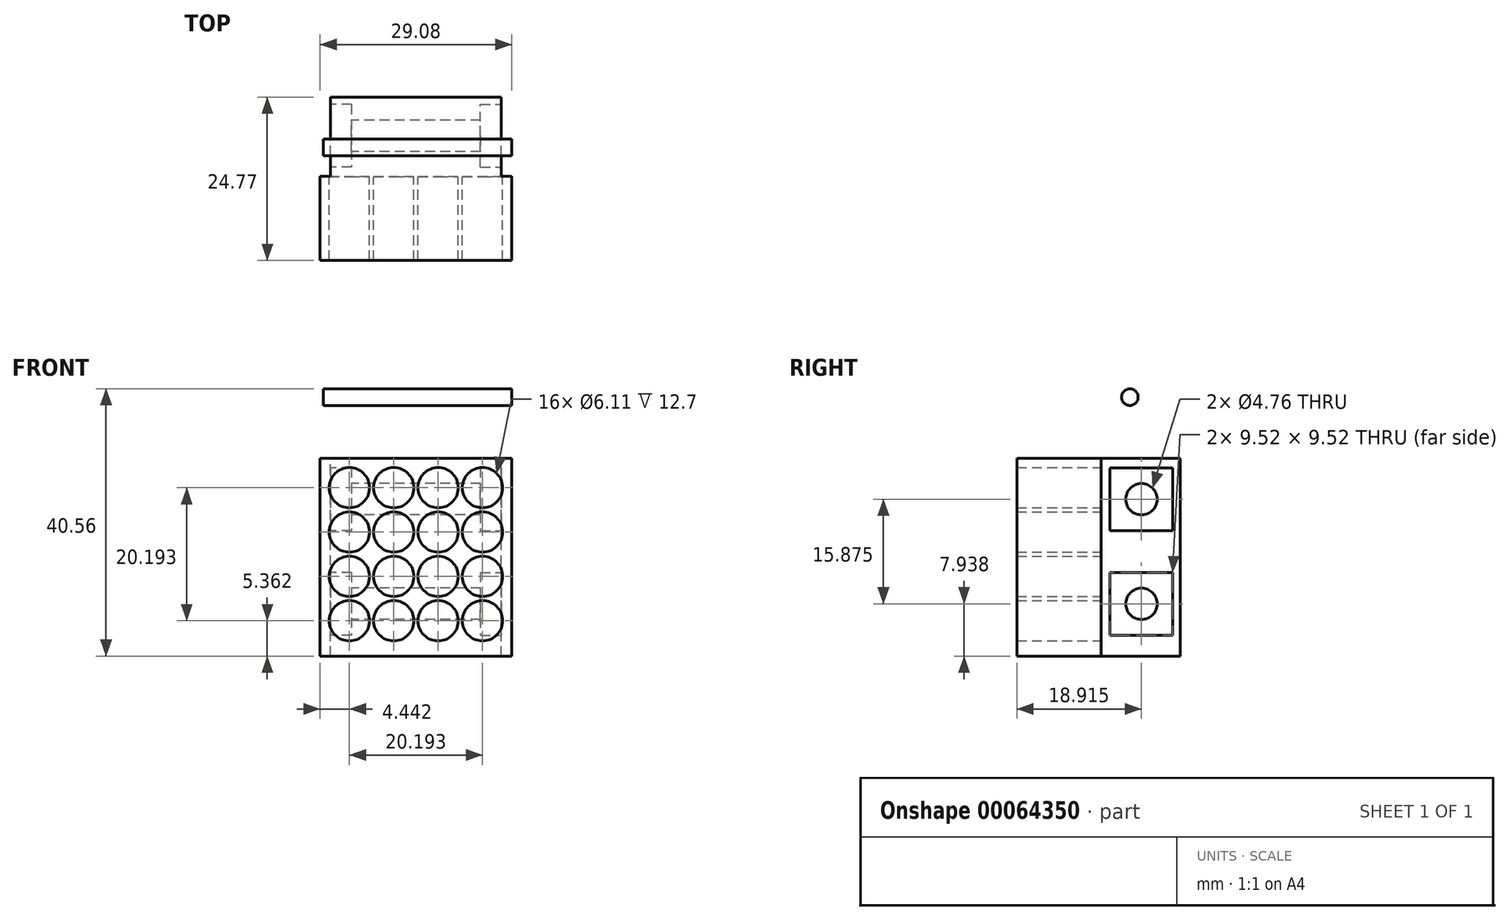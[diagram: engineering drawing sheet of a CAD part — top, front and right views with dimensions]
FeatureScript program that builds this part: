
annotation { "Feature Type Name" : "Feature", "Feature Type Description" : "" }
export const myFeature = defineFeature(function(context is Context, id is Id, definition is map)
    precondition{}
    {
        {
            var Q0;
            Q0=qCreatedBy(makeId("Front.planeOp"),FACE);
            var sketch = newSketch(context, id + "F0", { "sketchPlane" : qUnion([Q0])});
            skLineSegment(sketch, "E0.bottom", {"start": v(0, 0) * mm, "end": v(-29.08, 0) * mm});
            skLineSegment(sketch, "E0.top", {"start": v(0, 30) * mm, "end": v(-29.08, 30) * mm});
            skLineSegment(sketch, "E0.left", {"start": v(0, 0) * mm, "end": v(0, 30) * mm});
            skLineSegment(sketch, "E0.right", {"start": v(-29.08, 0) * mm, "end": v(-29.08, 30) * mm});
            skCircle(sketch, "E1", {"center": v(-4.45, 25.55) * mm, "radius": 3.06 * mm});
            skCircle(sketch, "E2.0.1.0", {"center": v(-4.45, 18.82) * mm, "radius": 3.06 * mm});
            skCircle(sketch, "E2.0.2.0", {"center": v(-4.45, 12.1) * mm, "radius": 3.06 * mm});
            skCircle(sketch, "E2.1.0.0", {"center": v(-11.18, 25.55) * mm, "radius": 3.06 * mm});
            skCircle(sketch, "E2.1.1.0", {"center": v(-11.18, 18.82) * mm, "radius": 3.06 * mm});
            skCircle(sketch, "E2.1.2.0", {"center": v(-11.18, 12.1) * mm, "radius": 3.06 * mm});
            skCircle(sketch, "E2.2.0.0", {"center": v(-17.9, 25.55) * mm, "radius": 3.06 * mm});
            skCircle(sketch, "E2.2.1.0", {"center": v(-17.9, 18.82) * mm, "radius": 3.06 * mm});
            skCircle(sketch, "E2.2.2.0", {"center": v(-17.9, 12.1) * mm, "radius": 3.06 * mm});
            skLineSegment(sketch, "E2.direction1", {"start": v(-4.45, 25.55) * mm, "end": v(-11.18, 25.55) * mm, "construction": true});
            skLineSegment(sketch, "E2.direction2", {"start": v(-4.45, 25.55) * mm, "end": v(-4.45, 18.82) * mm, "construction": true});
            skCircle(sketch, "E3.0.3.0", {"center": v(-24.64, 25.55) * mm, "radius": 3.06 * mm});
            skCircle(sketch, "E3.0.3.1", {"center": v(-24.64, 18.82) * mm, "radius": 3.06 * mm});
            skCircle(sketch, "E3.0.3.2", {"center": v(-24.64, 12.1) * mm, "radius": 3.06 * mm});
            skCircle(sketch, "E4.0.0.3", {"center": v(-4.45, 5.36) * mm, "radius": 3.06 * mm});
            skCircle(sketch, "E4.0.1.3", {"center": v(-11.18, 5.36) * mm, "radius": 3.06 * mm});
            skCircle(sketch, "E4.0.2.3", {"center": v(-17.9, 5.36) * mm, "radius": 3.06 * mm});
            skCircle(sketch, "E4.0.3.3", {"center": v(-24.64, 5.36) * mm, "radius": 3.06 * mm});
            skLineSegment(sketch, "E5", {"start": v(-29.08, 15) * mm, "end": v(0, 15) * mm, "construction": true});
            skSolve(sketch);
        }
        {
            var Q0;
            Q0=makeQuery(id+"F0.imprint","IMPRINT",FACE,{"disambiguationData":[TD([[makeQuery(id+"F0.imprint","IMPRINT",EDGE,{"derivedFrom":sQuery(id+"F0.wireOp",EDGE,"E0.bottom")}),-1.0]])]});
            extrude(context, id + "F1", {"entities" : qUnion([Q0]), "depth" : 12.7 * mm, "offsetDistance" : 25.4 * mm});
        }
        {
            var Q0;
            Q0=makeQuery(id+"F1.opExtrude","CAP_FACE",FACE,{"disambiguationData":[OSD([sQuery(id+"F0.wireOp",EDGE,"E0.bottom"),sQuery(id+"F0.wireOp",EDGE,"E0.top"),sQuery(id+"F0.wireOp",EDGE,"E0.left"),sQuery(id+"F0.wireOp",EDGE,"E0.right"),sQuery(id+"F0.wireOp",EDGE,"E1"),sQuery(id+"F0.wireOp",EDGE,"E2.0.1.0"),sQuery(id+"F0.wireOp",EDGE,"E2.0.2.0"),sQuery(id+"F0.wireOp",EDGE,"E2.1.0.0"),sQuery(id+"F0.wireOp",EDGE,"E2.1.1.0"),sQuery(id+"F0.wireOp",EDGE,"E2.1.2.0"),sQuery(id+"F0.wireOp",EDGE,"E2.2.0.0"),sQuery(id+"F0.wireOp",EDGE,"E2.2.1.0"),sQuery(id+"F0.wireOp",EDGE,"E2.2.2.0")])],"isStart":true});
            var sketch = newSketch(context, id + "F2", { "sketchPlane" : qUnion([Q0])});
            skLineSegment(sketch, "E6.bottom", {"start": v(0, 30) * mm, "end": v(29.08, 30) * mm});
            skLineSegment(sketch, "E6.top", {"start": v(0, 0) * mm, "end": v(29.08, 0) * mm});
            skLineSegment(sketch, "E6.left", {"start": v(0, 30) * mm, "end": v(0, 0) * mm});
            skLineSegment(sketch, "E6.right", {"start": v(29.08, 30) * mm, "end": v(29.08, 0) * mm});
            skSolve(sketch);
        }
        {
            var Q0;
            Q0=qSketchRegion(id+"F2",true);
            extrude(context, id + "F3", {"entities" : qUnion([Q0]), "operationType" : NewBodyOperationType.ADD, "depth" : 12.06 * mm, "offsetDistance" : 25.4 * mm});
        }
        {
            var Q0;
            Q0=makeQuery(id+"F3.boolean.opBoolean","MERGE",FACE,{"derivedFrom":[makeQuery(id+"F1.opExtrude","SWEPT_FACE",FACE,{"disambiguationData":[OSD([sQuery(id+"F0.wireOp",EDGE,"E0.left")])]}),makeQuery(id+"F3.opExtrude","SWEPT_FACE",FACE,{"disambiguationData":[OSD([sQuery(id+"F2.wireOp",EDGE,"E6.left")])]})]});
            var sketch = newSketch(context, id + "F4", { "sketchPlane" : qUnion([Q0])});
            skLineSegment(sketch, "E7.bottom", {"start": v(0.07, 0) * mm, "end": v(12.07, 0) * mm});
            skLineSegment(sketch, "E7.top", {"start": v(0.07, 30) * mm, "end": v(12.07, 30) * mm});
            skLineSegment(sketch, "E7.left", {"start": v(0.07, 0) * mm, "end": v(0.07, 30) * mm});
            skLineSegment(sketch, "E7.right", {"start": v(12.07, 0) * mm, "end": v(12.07, 30) * mm});
            skSolve(sketch);
        }
        {
            var Q0;
            Q0=qSketchRegion(id+"F4",true);
            extrude(context, id + "F5", {"entities" : qUnion([Q0]), "operationType" : NewBodyOperationType.REMOVE, "oppositeDirection" : true, "depth" : 1.59 * mm});
        }
        {
            var Q0;
            Q0=makeQuery(id+"F3.boolean.opBoolean","MERGE",FACE,{"derivedFrom":[makeQuery(id+"F1.opExtrude","SWEPT_FACE",FACE,{"disambiguationData":[OSD([sQuery(id+"F0.wireOp",EDGE,"E0.right")])]}),makeQuery(id+"F3.opExtrude","SWEPT_FACE",FACE,{"disambiguationData":[OSD([sQuery(id+"F2.wireOp",EDGE,"E6.right")])]})]});
            var sketch = newSketch(context, id + "F6", { "sketchPlane" : qUnion([Q0])});
            skLineSegment(sketch, "E8.bottom", {"start": v(-12.06, 0) * mm, "end": v(-0.06, 0) * mm});
            skLineSegment(sketch, "E8.top", {"start": v(-12.07, 30) * mm, "end": v(-0.07, 30) * mm});
            skLineSegment(sketch, "E8.left", {"start": v(-12.06, 0) * mm, "end": v(-12.07, 30) * mm});
            skLineSegment(sketch, "E8.right", {"start": v(-0.06, 0) * mm, "end": v(-0.07, 30) * mm});
            skSolve(sketch);
        }
        {
            var Q0;
            Q0=qSketchRegion(id+"F6",true);
            extrude(context, id + "F7", {"entities" : qUnion([Q0]), "operationType" : NewBodyOperationType.REMOVE, "oppositeDirection" : true, "depth" : 1.59 * mm});
        }
        {
            var Q0;
            Q0=makeQuery(id+"F7.boolean.opBoolean","COPY",FACE,{"derivedFrom":makeQuery(id+"F7.opExtrude","CAP_FACE",FACE,{"disambiguationData":[OSD([sQuery(id+"F6.wireOp",EDGE,"E8.bottom"),sQuery(id+"F6.wireOp",EDGE,"E8.top"),sQuery(id+"F6.wireOp",EDGE,"E8.left"),sQuery(id+"F6.wireOp",EDGE,"E8.right")])],"isStart":false})});
            var sketch = newSketch(context, id + "F8", { "sketchPlane" : qUnion([Q0])});
            skCircle(sketch, "E9", {"center": v(-6.21, 23.81) * mm, "radius": 2.38 * mm});
            skCircle(sketch, "E10", {"center": v(-6.21, 7.94) * mm, "radius": 2.38 * mm});
            skLineSegment(sketch, "E11", {"start": v(-6.22, 30) * mm, "end": v(-6.21, 0) * mm, "construction": true});
            skPoint(sketch, "E12", {"position": v(-6.22, 30) * mm});
            skSolve(sketch);
        }
        {
            var Q0;
            Q0=qSketchRegion(id+"F8",true);
            extrude(context, id + "F9", {"entities" : qUnion([Q0]), "operationType" : NewBodyOperationType.REMOVE, "endBound" : BoundingType.THROUGH_ALL, "oppositeDirection" : true, "depth" : 25.4 * mm});
        }
        {
            var Q0;
            Q0=makeQuery(id+"F7.boolean.opBoolean","COPY",FACE,{"derivedFrom":makeQuery(id+"F7.opExtrude","CAP_FACE",FACE,{"disambiguationData":[OSD([sQuery(id+"F6.wireOp",EDGE,"E8.bottom"),sQuery(id+"F6.wireOp",EDGE,"E8.top"),sQuery(id+"F6.wireOp",EDGE,"E8.left"),sQuery(id+"F6.wireOp",EDGE,"E8.right")])],"isStart":false})});
            var sketch = newSketch(context, id + "F10", { "sketchPlane" : qUnion([Q0])});
            skLineSegment(sketch, "E13.bottom", {"start": v(-10.98, 28.57) * mm, "end": v(-1.45, 28.57) * mm});
            skLineSegment(sketch, "E13.top", {"start": v(-10.98, 19.05) * mm, "end": v(-1.45, 19.05) * mm});
            skLineSegment(sketch, "E13.left", {"start": v(-10.98, 28.57) * mm, "end": v(-10.98, 19.05) * mm});
            skLineSegment(sketch, "E13.right", {"start": v(-1.45, 28.57) * mm, "end": v(-1.45, 19.05) * mm});
            skPoint(sketch, "E13.middle", {"position": v(-6.21, 23.81) * mm});
            skLineSegment(sketch, "E14.bottom", {"start": v(-10.98, 12.7) * mm, "end": v(-1.45, 12.7) * mm});
            skLineSegment(sketch, "E14.top", {"start": v(-10.98, 3.18) * mm, "end": v(-1.45, 3.18) * mm});
            skLineSegment(sketch, "E14.left", {"start": v(-10.98, 12.7) * mm, "end": v(-10.98, 3.18) * mm});
            skLineSegment(sketch, "E14.right", {"start": v(-1.45, 12.7) * mm, "end": v(-1.45, 3.18) * mm});
            skPoint(sketch, "E14.middle", {"position": v(-6.21, 7.94) * mm});
            skPoint(sketch, "E14.cornerSnap0", {"position": v(-10.98, 23.81) * mm});
            skSolve(sketch);
        }
        {
            var Q0;
            Q0=makeQuery(id+"F5.boolean.opBoolean","COPY",FACE,{"derivedFrom":makeQuery(id+"F5.opExtrude","CAP_FACE",FACE,{"disambiguationData":[OSD([sQuery(id+"F4.wireOp",EDGE,"E7.bottom"),sQuery(id+"F4.wireOp",EDGE,"E7.top"),sQuery(id+"F4.wireOp",EDGE,"E7.left"),sQuery(id+"F4.wireOp",EDGE,"E7.right")])],"isStart":false})});
            var sketch = newSketch(context, id + "F11", { "sketchPlane" : qUnion([Q0])});
            skLineSegment(sketch, "E15.bottom", {"start": v(1.45, 28.58) * mm, "end": v(10.98, 28.58) * mm});
            skLineSegment(sketch, "E15.top", {"start": v(1.45, 19.05) * mm, "end": v(10.98, 19.05) * mm});
            skLineSegment(sketch, "E15.left", {"start": v(1.45, 28.58) * mm, "end": v(1.45, 19.05) * mm});
            skLineSegment(sketch, "E15.right", {"start": v(10.98, 28.58) * mm, "end": v(10.98, 19.05) * mm});
            skPoint(sketch, "E15.middle", {"position": v(6.21, 23.81) * mm});
            skLineSegment(sketch, "E16.bottom", {"start": v(1.45, 12.7) * mm, "end": v(10.98, 12.7) * mm});
            skLineSegment(sketch, "E16.top", {"start": v(1.45, 3.17) * mm, "end": v(10.98, 3.17) * mm});
            skLineSegment(sketch, "E16.left", {"start": v(1.45, 12.7) * mm, "end": v(1.45, 3.17) * mm});
            skLineSegment(sketch, "E16.right", {"start": v(10.98, 12.7) * mm, "end": v(10.98, 3.17) * mm});
            skPoint(sketch, "E16.middle", {"position": v(6.21, 7.94) * mm});
            skSolve(sketch);
        }
        {
            var Q0;
            Q0 = qSketchRegion(id + "F10", true);
            extrude(context, id + "F12", {"entities" : qUnion([Q0]), "operationType" : NewBodyOperationType.REMOVE, "oppositeDirection" : true, "depth" : 3.17 * mm});
        }
        {
            var Q0;
            Q0 = qSketchRegion(id + "F11", true);
            extrude(context, id + "F13", {"entities" : qUnion([Q0]), "operationType" : NewBodyOperationType.REMOVE, "oppositeDirection" : true, "depth" : 3.17 * mm});
        }
        {
            var Q0;
            Q0=makeQuery(id+"F3.boolean.opBoolean","MERGE",FACE,{"derivedFrom":[makeQuery(id+"F1.opExtrude","SWEPT_FACE",FACE,{"disambiguationData":[OSD([sQuery(id+"F0.wireOp",EDGE,"E0.left")])]}),makeQuery(id+"F3.opExtrude","SWEPT_FACE",FACE,{"disambiguationData":[OSD([sQuery(id+"F2.wireOp",EDGE,"E6.left")])]})]});
            var sketch = newSketch(context, id + "F14", { "sketchPlane" : qUnion([Q0])});
            skCircle(sketch, "E17", {"center": v(4.45, 39.3) * mm, "radius": 1.26 * mm});
            skSolve(sketch);
        }
        {
            var Q0;
            Q0 = qSketchRegion(id + "F14", true);
            var Q1;
            Q1=sQuery(id+"F14.wireOp",EDGE,"E17");
            extrude(context, id + "F15", {"entities" : qUnion([Q0]), "surfaceEntities" : qUnion([Q1]), "oppositeDirection" : true, "depth" : 28.57 * mm, "offsetDistance" : 25.4 * mm});
        }
    });
